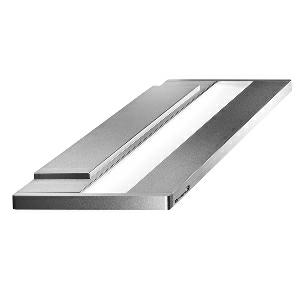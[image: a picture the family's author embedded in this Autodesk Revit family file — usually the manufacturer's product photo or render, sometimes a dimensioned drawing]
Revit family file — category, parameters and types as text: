
# Revit family: zera_bed_-_zew_9000_830_-_ul_re_lvc_nl_00812996_8b03
name_source: partatom
category: Lighting Fixtures
units: mm (PartAtom-declared; Revit-internal decimal feet)

## family parameters
Cut with Voids When Loaded = No
Host = Face
Light Source = No
Part Type = Normal
Room Calculation Point = No
Round Connector Dimension = Use Diameter
Shared = No

## types (1)
- AL+UL (1 x LED, 7600 lm, 4000K/3000K)
    Apparent Load = 76 VA
    Approval mark = CE
    CIE Flux Codes = 45 81 99 31 100
    Color Rendering = 90/80
    Color Temperature = 4000K/3000K
    Default Elevation = 2000 mm  [stored 6.56168 ft]
    Description = ZEW 9000/830|Wall-mounted luminaire|light source:   Warm white   |work equipment: Power supply unit|luminous flux: 8960 lm|light distribution: Direct/indirect|class of protection: I|technology: Switchable|mains lead: Connector 5 pin|glare control: Diffusor|special features: General light, indirect, 3000K, Ra80, DIN EN 60598-2-25, Reading light, direct, 2700K, Ra90, indir, Switch right, Protective low voltage relay (LVC), dir 4K 36W Ra95|
    Frequency = 50 Hz, 60 Hz
    Height = 20 mm  [stored 0.0656168 ft]
    Lamp = 1 x LED
    Lamp Light Flux = 7600 lm
    Lamp count = 1
    Length = 1050 mm
    Luminous efficacy = 100 lm/W
    Manufacturer = Waldmann
    ModVariant = No
    Model = 00812996
    Mounting Place = Wall
    Mounting Type = Surface mounted
    Number of Poles = 1
    OnlyDefault = Yes
    Power Factor = 1
    Product Name = ZERA.bed - ZEW 9000/830 - UL RE/LVC/NL
    Product group = Wall mounted Luminaire
    ProductGroupID = 20
    Protection Class = Protection class I
    Protection Degree = IP 20
    RLX_Detail_Level = 1
    RLX_Emergency_Light_Flux = 0 lm
    RLX_Emergency_Type = 0
    RLX_Emergency_Type_DB = No
    RlxData = <blob elided: 62877 chars, md5=75dbcc45>
    Socket = socket
    Standby Power = 0 W
    System Light Flux = 7600 lm
    System Power = 76 W
    Type Comments = General and Examation Light
    Type Image = zera_bed.jpg
    URL = http://relux.com
    VarID = al_ul_37f9
    Voltage = 230 V
    Voltage Range = 220-240 V
    Weight = 0.00 kg
    Width = 230 mm

note: [stored X ft] marks values corroborated as IEEE doubles in the binary element streams (Revit-internal decimal feet)

## geometry (parser evidence)
native form markers: Blend x4, Sweep x14
no freeform markers — native parametric forms only
